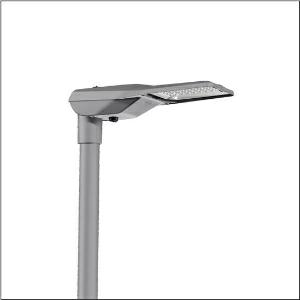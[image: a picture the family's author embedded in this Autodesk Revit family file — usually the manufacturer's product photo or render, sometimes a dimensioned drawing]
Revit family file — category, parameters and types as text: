
# Revit family: streetlight_sl_21_iq_mini___st1_0a_5xe2d51y08gb_2a2c
name_source: partatom
category: Lighting Fixtures
units: mm (PartAtom-declared; Revit-internal decimal feet)

## family parameters
Cut with Voids When Loaded = No
Host = Face
Light Source = No
Part Type = Normal
Room Calculation Point = No
Round Connector Dimension = Use Diameter
Shared = No

## types (1)
- --- (1 x LED, 5260 lm, 39.8 W, 3000K)
    Apparent Load = 40 VA
    CIE Flux Codes = 37 72 97 100 100
    Color Rendering = 80
    Color Temperature = 3000K
    Default Elevation = 1800 mm
    Description = Streetlight SL 21 iQ mini, mast luminaire, primary light control with lens, of PMMA, primary optical cover: cover, of toughened safety glass, transparent, light distribution: ST1.0a, light emission: direct distribution, primary light characteristic: asymmetric, installation type: post-top, side-entry, LED, High Power LED, rated luminous flux: 5.260lm, luminous efficacy: 132lm/W, light colour: 830, colour temperature: 3000K, control: presetting dimming logarithmic, Street-Remote, Auto-Match, Temp-Guard, Lumen-Switch, Night-Set, Smart-Wire, Light-Fading, Desk-Remote (wireless, voltage-free reading and setting of iQ features in the workshop via application-optimized NFC function/RFID function), optimised constant luminous flux control (CLO 2.0), mains connection: 220..240V, AC, 50/60Hz, start of lifetime: 40W, end of service life: 41W, reduction: 18W, luminaire housing, of diecast aluminium, powder-coated, Siteco® metallic grey (DB 702S), corrosivity category C5 mid according to DIN EN ISO 12944, please order mast flange separately, inclination adjustable: 0°, 5°, 10°, 15°, sealing non-destructively replaceable, multi-level sealing system, length: 628mm, width: 235mm, height: 110mm, mast flange for spigot size: 42mm (side-entry): 5XC10008XM4, 60/48mm (side-entry/post-top): 5XC10108XM2, 76/60mm (side-entry/post-top): 5XC10108XM1, Smart Interface below and above, protection rating (complete): IP66, insulation class (complete): insulation class II (safety insulation), certification: CE, ENEC, ENEC+, VDE, impact resistance: IK09, permissible operating ambient temperature for outdoor applications: -40..+50°C, standard-compliant lighting for roads and squares, packaging unit: 1 piece

Light Distribution: ST1.0a
    Height = 110 mm
    Lamp = 1 x LED
    Lamp Light Flux = 5260 lm
    Lamp Power = 39.8 W
    Lamp count = 1
    Length = 625 mm
    Luminous efficacy = 132 lm/W
    Manufacturer = Siteco
    ModVariant = No
    Model = 5XE2D51Y08GB
    Number of Poles = 1
    OnlyDefault = Yes
    Power Factor = 1
    Product Name = Streetlight SL 21 iQ mini | ST1.0a
    Product group = mast luminaire | pylon top
    ProductGroupID = 6100
    Protection Class = Protection class II
    Protection Degree = IP 66
    RLX_Detail_Level = 1
    RLX_Emergency_Light_Flux = 0 lm
    RLX_Emergency_Type = 0
    RLX_Emergency_Type_DB = No
    RlxData = <blob elided: 92441 chars, md5=132d6650>
    Socket = socket
    Standby Power = 0 W
    System Light Flux = 5260 lm
    System Power = 40 W
    Type Comments = factory setting: luminous flux: 100 % | dim-lin: 254 | 800 mA
    Type Image = l_1003514.jpg
    URL = http://relux.com
    VarID = @adj_063033
    Voltage = 0 V
    Weight = 0.00 kg
    Width = 234 mm

## geometry (parser evidence)
native form markers: Blend x4, Sweep x11
no freeform markers — native parametric forms only
